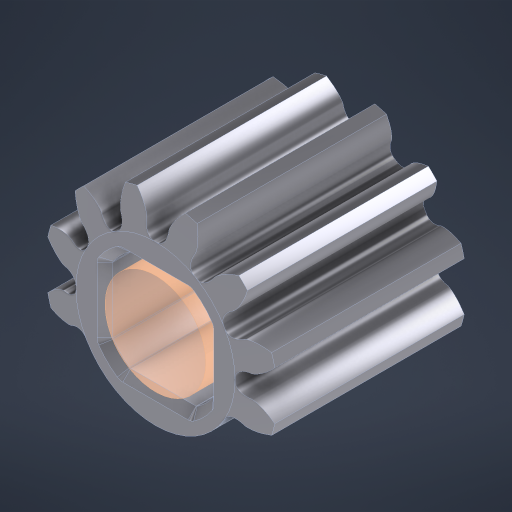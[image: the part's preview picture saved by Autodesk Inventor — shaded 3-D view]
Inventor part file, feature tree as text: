
AUTODESK INVENTOR PART (.ipt)
format: ipt  version: 2024 (Build 280153000, 153)  size: 565,248 bytes
history: native  units: in
note: dims shown in document units (in); Inventor stores cm internally (conversion verified against a paired STEP export)
features: extrude x2, sketch x2, other x1
ambient origin geometry x8: Origin, YZ Plane, XZ Plane, XY Plane, X Axis, Y Axis, Z Axis, Center Point
bodies: Solid1 (feature_tree), Body1 (feature_tree)
feature tree (5):
  extrude  "Extrusion1"  TaperAngle=0.0deg  [1 undecoded]
  sketch  "Sketch1"  dims[d0=1.0in d1=0.0in d2=0.0in d3=0.0in]
  other  "Srf1"
  sketch  "Sketch2"
  extrude  "ExtrusionSrf1"  [1 undecoded]
note: 2 required parameter values undecoded (feature->parameter linkage not recoverable at this tier; creation-order binding heuristic only, values carry confidence <= 0.55)
